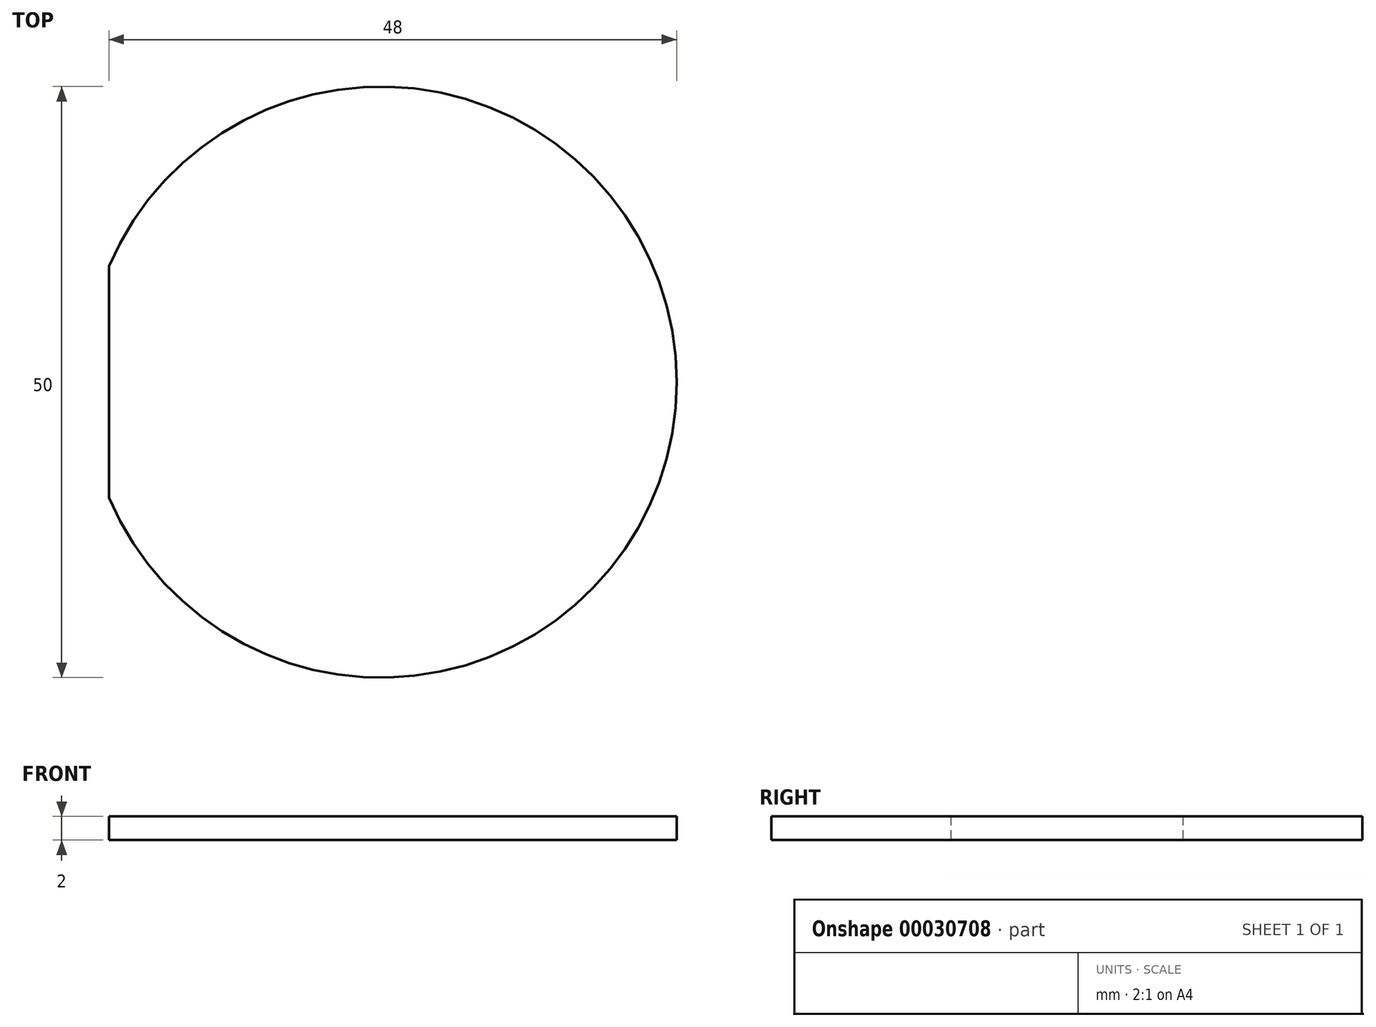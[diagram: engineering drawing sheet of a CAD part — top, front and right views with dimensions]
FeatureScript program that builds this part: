
annotation { "Feature Type Name" : "Feature", "Feature Type Description" : "" }
export const myFeature = defineFeature(function(context is Context, id is Id, definition is map)
    precondition{}
    {
        {
            var Q0;
            Q0=qCreatedBy(makeId("Top.planeOp"),FACE);
            var sketch = newSketch(context, id + "F0", { "sketchPlane" : qUnion([Q0])});
            skCircle(sketch, "E0", {"center": v(0, 0) * mm, "radius": 25 * mm});
            skLineSegment(sketch, "E1", {"start": v(-23, 9.8) * mm, "end": v(-23, -9.8) * mm});
            skSolve(sketch);
        }
        {
            var Q0;
            {var subQ0=sQuery(id+"F0.wireOp",EDGE,"E1");Q0=makeQuery(id+"F0.imprint","IMPRINT",FACE,{"disambiguationData":[TD([[makeQuery(id+"F0.imprint","IMPRINT",EDGE,{"derivedFrom":subQ0}),1.0]])]});}
            extrude(context, id + "F1", {"entities" : qUnion([Q0]), "depth" : 2 * mm});
        }
    });
